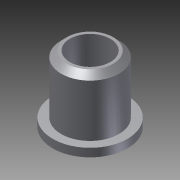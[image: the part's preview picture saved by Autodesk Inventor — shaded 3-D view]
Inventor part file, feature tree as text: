
AUTODESK INVENTOR PART (.ipt)
format: ipt  version: 2011 SP1 (Build 150282100, 282)  size: 139,776 bytes
history: native  units: in
note: dims shown in document units (in); Inventor stores cm internally (conversion verified against a paired STEP export)
features: other x35, sketch x5, extrude x3, revolve x1, hole x1
ambient origin geometry x8: Origin, YZ Plane, XZ Plane, XY Plane, X Axis, Y Axis, Z Axis, Center Point
bodies: Solid1 (feature_tree)
feature tree (45):
  extrude  "Extrusion1"  TaperAngle=360.0deg  [1 undecoded]
  revolve  "Revolution1"  [1 undecoded]
  extrude  "Extrusion2"  [1 undecoded]
  hole  "Drilling 1"  [1 undecoded]
  extrude  "Extrusion3"  [1 undecoded]
  other  "1_XY"
  other  "1_YZ"
  other  "1_ZX"
  other  "1_X"
  other  "1_Y"
  other  "1_Z"
  other  "1_Center"
  other  "2_XY"
  other  "2_YZ"
  other  "2_ZX"
  other  "2_X"
  other  "2_Y"
  other  "2_Z"
  other  "2_Center"
  other  "3_XY"
  other  "3_YZ"
  other  "3_ZX"
  other  "3_X"
  other  "3_Y"
  other  "3_Z"
  other  "3_Center"
  other  "4_XY"
  other  "4_YZ"
  other  "4_ZX"
  other  "4_X"
  other  "4_Y"
  other  "4_Z"
  other  "4_Center"
  other  "to_base_XY"
  other  "to_base_YZ"
  other  "to_base_ZX"
  other  "to_base_X"
  other  "to_base_Y"
  other  "to_base_Z"
  other  "to_base_Center"
  sketch  "Sketch_1"  dims[d0=0.512in d1=0.0in d2=360.0deg]
  sketch  "Sketch_7"
  sketch  "Sketch_8"
  sketch  "Sketch4"  dims[d5=0.1708in d6=0.75in d7=0.375in d8=0.25in d9=0.5635in d10=0.31in d11=0.0in d12=0.512in d13=0.0in]
  sketch  "Sketch_2"  dims[d3=0.3135in d4=0.0in]
note: 5 required parameter values undecoded (feature->parameter linkage not recoverable at this tier; creation-order binding heuristic only, values carry confidence <= 0.55)